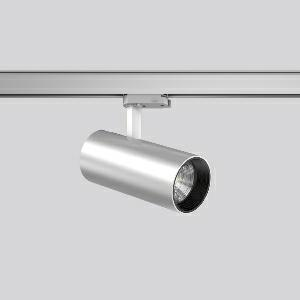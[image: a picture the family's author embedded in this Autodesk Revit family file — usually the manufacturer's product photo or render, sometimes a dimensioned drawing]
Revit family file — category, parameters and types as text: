
# Revit family: deecos_s_mini_742208_004_3_ffee
name_source: partatom
category: Lighting Fixtures
units: mm (PartAtom-declared; Revit-internal decimal feet)

## family parameters
Cut with Voids When Loaded = No
Host = Face
Light Source = No
Part Type = Normal
Room Calculation Point = No
Round Connector Dimension = Use Diameter
Shared = No

## types (1)
- DEECOS S mini (1 x LED Modul 935, 2900 lm, 3500)
    Apparent Load = 29 VA
    Approval mark = CE
    CIE Flux Codes = 98 100 100 100 100
    Color Rendering = 92
    Color Temperature = 3500
    Default Elevation = 1800 mm
    Description = Series: DEECOS S mini
LED surface-mounted projector in modern design with no visible cooling ribs. Housing: die-cast aluminium, powder-coated. Rotation range: 356°. Swivel range: 90°. Black plastic ring and recessed LED to prevent glare from the side. Optical assembly with lens made of plastic (polycarbonate) for the best homogeneous light distribution - can be changed without tools. Best colour rendering index Ra>90. With multi adaptor for 3-circuit tracks 230 V. Suitable for Track on ceiling, Wall track. High quality converter without flickering and stroboscopic effect. The following accessories can be mounted without use of tools: interchangeable lenses, decorative glasses, honeycomb louvre, clear and frosted diffusers, white interchangeable plastic ring. 
Colour: silver
Diameter: 87 mm
Height: 214 mm
Lamp: LED
Socket: without socket
Colour temperature: 3500K
Colour rendering index (CRI): 92
System power: 29 W
Rated luminous flux: 2900 lm
Luminous efficiency: 100 lm/W
Control gear: Regulated power supply
Protection class: I
Type of protection: IP 20
    Height = 214 mm
    Lamp = 1 x LED Modul 935
    Lamp Light Flux = 2900 lm
    Lamp count = 1
    Length = 87 mm
    Lifetime = 50000 h
    Luminous efficacy = 100 lm/W
    Manufacturer = RZB
    ModVariant = No
    Model = 742208.004.3
    Mounting Place = Ceiling
    Mounting Type = Rail mounted
    Number of Poles = 1
    OnlyDefault = Yes
    Power Factor = 1
    Product Name = DEECOS S mini
    Product group = Track mounted projectors
    ProductGroupID = 301
    Protection Class = Protection class I
    Protection Degree = IP 20
    RLX_Detail_Level = 1
    RLX_Emergency_Light_Flux = 0 lm
    RLX_Emergency_Type = 0
    RLX_Emergency_Type_DB = No
    RlxData = <blob elided: 37513 chars, md5=3809c4a0>
    Socket = socket
    Standby Power = 0 W
    System Light Flux = 2900 lm
    System Power = 29 W
    Type Comments = Product without accessories
    Type Image = 741930.004.jpg
    URL = http://relux.com
    VarID = ---
    Voltage = 230 V
    Voltage Range = 220-240 V
    Weight = 0.00 kg
    Width = 0 mm  [stored 0 ft]

note: [stored X ft] marks values corroborated as IEEE doubles in the binary element streams (Revit-internal decimal feet)

## geometry (parser evidence)
native form markers: Blend x4, Sweep x13
no freeform markers — native parametric forms only
